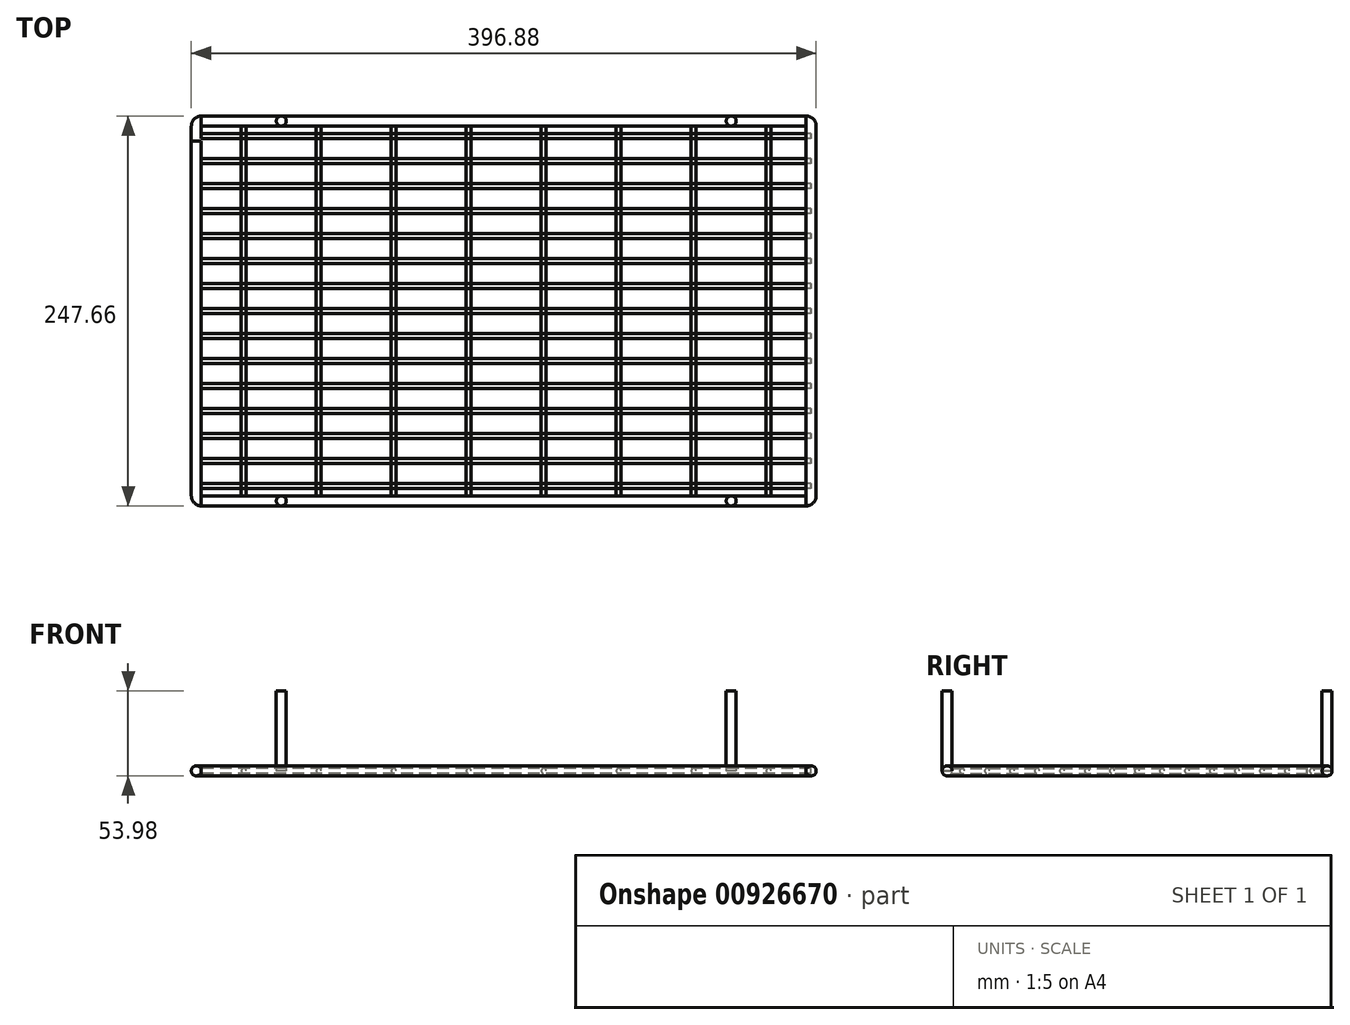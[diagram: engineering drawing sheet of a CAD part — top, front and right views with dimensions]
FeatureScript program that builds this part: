
annotation { "Feature Type Name" : "Feature", "Feature Type Description" : "" }
export const myFeature = defineFeature(function(context is Context, id is Id, definition is map)
    precondition{}
    {
        {
            var Q0;
            Q0=qCreatedBy(makeId("Right.planeOp"),FACE);
            var sketch = newSketch(context, id + "F0", { "sketchPlane" : qUnion([Q0])});
            skCircle(sketch, "E0", {"center": v(120.65, 0) * mm, "radius": 3.18 * mm});
            skCircle(sketch, "E1", {"center": v(-120.65, 0) * mm, "radius": 3.18 * mm});
            skSolve(sketch);
        }
        {
            var Q0;
            Q0 = qSketchRegion(id + "F0", true);
            extrude(context, id + "F1", {"entities" : qUnion([Q0]), "depth" : 384.17 * mm, "offsetDistance" : 25.4 * mm});
        }
        {
            var Q0;
            Q0=qCreatedBy(makeId("Top.planeOp"),FACE);
            var sketch = newSketch(context, id + "F2", { "sketchPlane" : qUnion([Q0])});
            skLineSegment(sketch, "E2", {"start": v(0, 120.65) * mm, "end": v(0, 120.65) * mm});
            skLineSegment(sketch, "E3", {"start": v(-3.18, 117.48) * mm, "end": v(-3.18, 107.95) * mm});
            skPoint(sketch, "E4.visualSharp", {"position": v(-3.17, 120.65) * mm});
            skArc(sketch, "E4.filletArc", {"start": v(0, 120.65) * mm, "mid": v(-2.25, 119.72) * mm, "end": v(-3.17, 117.48) * mm});
            skLineSegment(sketch, "E5", {"start": v(0, -120.65) * mm, "end": v(0, -120.65) * mm});
            skSolve(sketch);
        }
        {
            var Q0;
            Q0=makeQuery(id+"F1.opExtrude","CAP_FACE",FACE,{"disambiguationData":[OSD([sQuery(id+"F0.wireOp",EDGE,"E0")])],"isStart":true});
            var Q1;
            Q1=sQuery(id+"F2.wireOp",EDGE,"E4.filletArc");
            var Q2;
            Q2=sQuery(id+"F2.wireOp",EDGE,"E3");
            sweep(context, id + "F3", {"profiles" : qUnion([Q0]), "path" : qUnion([Q1, Q2])});
        }
        {
            var Q0;
            Q0=qCreatedBy(makeId("Top.planeOp"),FACE);
            var sketch = newSketch(context, id + "F4", { "sketchPlane" : qUnion([Q0])});
            skLineSegment(sketch, "E6", {"start": v(0, -120.65) * mm, "end": v(0, -120.65) * mm});
            skLineSegment(sketch, "E7", {"start": v(-3.18, -117.48) * mm, "end": v(-3.18, 107.95) * mm});
            skPoint(sketch, "E8.visualSharp", {"position": v(-3.18, -120.65) * mm});
            skArc(sketch, "E8.filletArc", {"start": v(-3.18, -117.48) * mm, "mid": v(-2.25, -119.72) * mm, "end": v(0, -120.65) * mm});
            skSolve(sketch);
        }
        {
            var Q0;
            Q0=makeQuery(id+"F1.opExtrude","CAP_FACE",FACE,{"disambiguationData":[OSD([sQuery(id+"F0.wireOp",EDGE,"E1")])],"isStart":true});
            var Q1;
            Q1 = qConstructionFilter(qBodyType(qCreatedBy(id + "F4" ,EDGE), BodyType.WIRE), ConstructionObject.NO);
            sweep(context, id + "F5", {"profiles" : qUnion([Q0]), "path" : qUnion([Q1])});
        }
        {
            var Q0;
            Q0=qCreatedBy(makeId("Top.planeOp"),FACE);
            var sketch = newSketch(context, id + "F6", { "sketchPlane" : qUnion([Q0])});
            skLineSegment(sketch, "E9", {"start": v(384.18, 120.65) * mm, "end": v(384.18, 120.65) * mm});
            skLineSegment(sketch, "E10", {"start": v(387.35, 117.48) * mm, "end": v(387.35, -117.47) * mm});
            skLineSegment(sketch, "E11", {"start": v(384.18, -120.65) * mm, "end": v(384.18, -120.65) * mm});
            skPoint(sketch, "E12.visualSharp", {"position": v(387.35, -120.65) * mm});
            skArc(sketch, "E12.filletArc", {"start": v(384.18, -120.65) * mm, "mid": v(386.42, -119.72) * mm, "end": v(387.35, -117.47) * mm});
            skPoint(sketch, "E13.visualSharp", {"position": v(387.35, 120.65) * mm});
            skArc(sketch, "E13.filletArc", {"start": v(387.35, 117.48) * mm, "mid": v(386.42, 119.72) * mm, "end": v(384.18, 120.65) * mm});
            skSolve(sketch);
        }
        {
            var Q0;
            Q0=makeQuery(id+"F1.opExtrude","CAP_FACE",FACE,{"disambiguationData":[OSD([sQuery(id+"F0.wireOp",EDGE,"E0")])],"isStart":false});
            var Q1;
            Q1 = qConstructionFilter(qBodyType(qCreatedBy(id + "F6" ,EDGE), BodyType.WIRE), ConstructionObject.NO);
            sweep(context, id + "F7", {"profiles" : qUnion([Q0]), "path" : qUnion([Q1])});
        }
        {
            var Q0;
            Q0=qCreatedBy(makeId("Front.planeOp"),FACE);
            var sketch = newSketch(context, id + "F8", { "sketchPlane" : qUnion([Q0])});
            skCircle(sketch, "E14", {"center": v(26.99, 0) * mm, "radius": 1.59 * mm});
            skCircle(sketch, "E15", {"center": v(74.61, 0) * mm, "radius": 1.59 * mm});
            skCircle(sketch, "E16", {"center": v(122.24, 0) * mm, "radius": 1.59 * mm});
            skCircle(sketch, "E17", {"center": v(169.86, 0) * mm, "radius": 1.59 * mm});
            skCircle(sketch, "E18", {"center": v(217.49, 0) * mm, "radius": 1.59 * mm});
            skCircle(sketch, "E19", {"center": v(265.11, 0) * mm, "radius": 1.59 * mm});
            skCircle(sketch, "E20", {"center": v(312.74, 0) * mm, "radius": 1.59 * mm});
            skCircle(sketch, "E21", {"center": v(360.36, 0) * mm, "radius": 1.59 * mm});
            skSolve(sketch);
        }
        {
            var Q0;
            Q0 = qSketchRegion(id + "F8", true);
            extrude(context, id + "F9", {"entities" : qUnion([Q0]), "depth" : 117.47 * mm, "offsetDistance" : 25.4 * mm, "hasSecondDirection" : true, "secondDirectionOppositeDirection" : true, "secondDirectionDepth" : 117.47 * mm});
        }
        {
            var Q0;
            Q0=qCreatedBy(makeId("Right.planeOp"),FACE);
            var sketch = newSketch(context, id + "F10", { "sketchPlane" : qUnion([Q0])});
            skCircle(sketch, "E22", {"center": v(-111.13, 0) * mm, "radius": 1.59 * mm});
            skCircle(sketch, "E23", {"center": v(-95.25, 0) * mm, "radius": 1.59 * mm});
            skCircle(sketch, "E24", {"center": v(-79.38, 0) * mm, "radius": 1.59 * mm});
            skCircle(sketch, "E25", {"center": v(-63.5, 0) * mm, "radius": 1.59 * mm});
            skCircle(sketch, "E26", {"center": v(-47.63, 0) * mm, "radius": 1.59 * mm});
            skCircle(sketch, "E27", {"center": v(-31.75, 0) * mm, "radius": 1.59 * mm});
            skCircle(sketch, "E28", {"center": v(-15.88, 0) * mm, "radius": 1.59 * mm});
            skCircle(sketch, "E29", {"center": v(0, 0) * mm, "radius": 1.59 * mm});
            skCircle(sketch, "E30", {"center": v(15.87, 0) * mm, "radius": 1.59 * mm});
            skCircle(sketch, "E31", {"center": v(31.75, 0) * mm, "radius": 1.59 * mm});
            skCircle(sketch, "E32", {"center": v(47.62, 0) * mm, "radius": 1.59 * mm});
            skCircle(sketch, "E33", {"center": v(63.5, 0) * mm, "radius": 1.59 * mm});
            skCircle(sketch, "E34", {"center": v(79.37, 0) * mm, "radius": 1.59 * mm});
            skCircle(sketch, "E35", {"center": v(95.25, 0) * mm, "radius": 1.59 * mm});
            skCircle(sketch, "E36", {"center": v(111.12, 0) * mm, "radius": 1.59 * mm});
            skSolve(sketch);
        }
        {
            var Q0;
            Q0 = qSketchRegion(id + "F10", true);
            extrude(context, id + "F11", {"entities" : qUnion([Q0]), "depth" : 387.35 * mm, "offsetDistance" : 25.4 * mm});
        }
        {
            var Q0;
            Q0=qCreatedBy(makeId("Top.planeOp"),FACE);
            var sketch = newSketch(context, id + "F12", { "sketchPlane" : qUnion([Q0])});
            skCircle(sketch, "E37", {"center": v(50.8, -120.65) * mm, "radius": 3.18 * mm});
            skCircle(sketch, "E38", {"center": v(336.55, -120.65) * mm, "radius": 3.18 * mm});
            skCircle(sketch, "E39", {"center": v(50.8, 120.65) * mm, "radius": 3.18 * mm});
            skCircle(sketch, "E40", {"center": v(336.55, 120.65) * mm, "radius": 3.18 * mm});
            skSolve(sketch);
        }
        {
            var Q0;
            Q0 = qSketchRegion(id + "F12", true);
            extrude(context, id + "F13", {"entities" : qUnion([Q0]), "depth" : 50.8 * mm, "offsetDistance" : 25.4 * mm});
        }
    });
